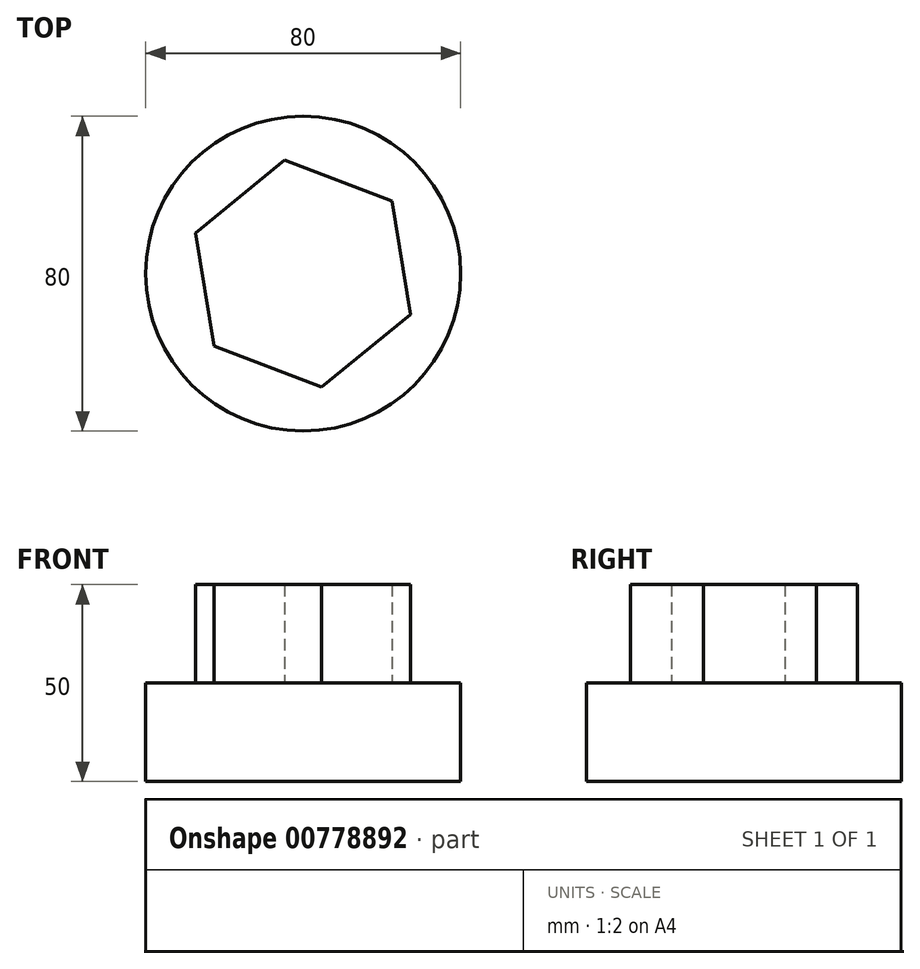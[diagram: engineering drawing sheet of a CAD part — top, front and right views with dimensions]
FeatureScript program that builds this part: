
annotation { "Feature Type Name" : "Feature", "Feature Type Description" : "" }
export const myFeature = defineFeature(function(context is Context, id is Id, definition is map)
    precondition{}
    {
        {
            var Q0;
            Q0=qCreatedBy(makeId("Top.planeOp"),FACE);
            var sketch = newSketch(context, id + "F0", { "sketchPlane" : qUnion([Q0])});
            skCircle(sketch, "E0", {"center": v(0, 0) * mm, "radius": 40 * mm});
            skSolve(sketch);
        }
        {
            var Q0;
            Q0=makeQuery(id+"F0.imprint","IMPRINT",FACE,{"disambiguationData":[TD([[makeQuery(id+"F0.imprint","IMPRINT",EDGE,{"derivedFrom":sQuery(id+"F0.wireOp",EDGE,"E0")}),1.0]])]});
            extrude(context, id + "F1", {"entities" : qUnion([Q0]), "depth" : 25 * mm, "offsetDistance" : 25 * mm});
        }
        {
            var Q0;
            Q0=makeQuery(id+"F1.opExtrude","CAP_FACE",FACE,{"disambiguationData":[OSD([sQuery(id+"F0.wireOp",EDGE,"E0")])],"isStart":false});
            var sketch = newSketch(context, id + "F2", { "sketchPlane" : qUnion([Q0])});
            skCircle(sketch, "E1.cCircle", {"center": v(0, 0) * mm, "radius": 25.27 * mm, "construction": true});
            skLineSegment(sketch, "E1.0", {"start": v(-27.28, 10.35) * mm, "end": v(-4.67, 28.8) * mm});
            skLineSegment(sketch, "E1.1", {"start": v(-4.67, 28.8) * mm, "end": v(22.6, 18.45) * mm});
            skLineSegment(sketch, "E1.2", {"start": v(22.6, 18.45) * mm, "end": v(27.28, -10.35) * mm});
            skLineSegment(sketch, "E1.3", {"start": v(27.28, -10.35) * mm, "end": v(4.67, -28.8) * mm});
            skLineSegment(sketch, "E1.4", {"start": v(4.67, -28.8) * mm, "end": v(-22.6, -18.45) * mm});
            skLineSegment(sketch, "E1.5", {"start": v(-22.6, -18.45) * mm, "end": v(-27.28, 10.35) * mm});
            skPoint(sketch, "E1.0.midPoint", {"position": v(-15.98, 19.57) * mm});
            skSolve(sketch);
        }
        {
            var Q0;
            Q0=makeQuery(id+"F2.imprint","IMPRINT",FACE,{"disambiguationData":[TD([[makeQuery(id+"F2.imprint","IMPRINT",EDGE,{"derivedFrom":sQuery(id+"F2.wireOp",EDGE,"E1.0")}),-1.0]])]});
            extrude(context, id + "F3", {"entities" : qUnion([Q0]), "operationType" : NewBodyOperationType.ADD, "depth" : 25 * mm, "offsetDistance" : 25 * mm});
        }
    });
